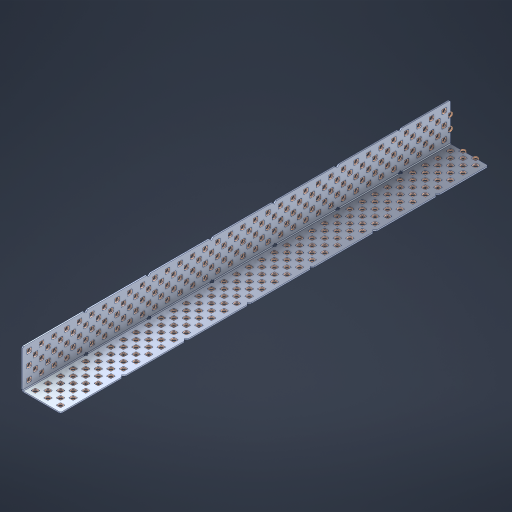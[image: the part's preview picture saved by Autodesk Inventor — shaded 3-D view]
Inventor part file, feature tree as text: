
AUTODESK INVENTOR PART (.ipt)
format: ipt  version: 2023 (Build 270158000, 158)  size: 3,338,752 bytes
history: native  units: in
note: dims shown in document units (in); Inventor stores cm internally (conversion verified against a paired STEP export)
features: other x346, extrude x338, sheet_metal_op x8, sketch x7, pattern_linear x3, mirror x1, chamfer x1
ambient origin geometry x8: Origin, YZ Plane, XZ Plane, XY Plane, X Axis, Y Axis, Z Axis, Center Point
bodies: Solid1 (feature_tree), Body (feature_tree)
feature tree (704):
  sheet_metal_op  "Flanges"
  sheet_metal_op  "Body Pattern"
  pattern_linear  "Center Double"  Spacing1=1.5in  [1 undecoded]
  pattern_linear  "Center Pattern"  Spacing1=0.1875in  [1 undecoded]
  other  "Arc Length"
  pattern_linear  "Notch Pattern"  Spacing1=0.0469in  [1 undecoded]
  other  "Diagonal Plane"
  mirror  "Everything Mirrored"
  chamfer  "End Chamfer"
  sketch  "Sketch1"  dims[d0=1.5in]
  other  "Plate1"
  sketch  "Sketch2"  dims[d1=17.0in]
  other  "Plate2"
  sheet_metal_op  "Bend1"
  sheet_metal_op  "Corner1"
  sketch  "Sketch8"  dims[d2=0.0469in]
  sketch  "Sketch9"  dims[d3=0.0469in]
  other  "Srf91"
  sheet_metal_op  "Body Pattern Sketch"
  other  "Srf92"
  sketch  "Sketch13"  dims[d4=0.0234in]
  sketch  "Sketch15"  dims[d5=0.0938in]
  sketch  "Sketch16"  dims[d6=0.0469in d7=1.5in d8=90.0deg d9=0.0312in d10=0.1875in d11=0.0469in d12=0.0469in d49=0.182in d50=0.02in d52=0.25in d53=0.0469in d54=0.0in d55=0.172in d56=1.0in d57=0.0in d85=0.1473in d86=0.1659in d89=0.0469in d90=0.0in d91=0.04in d92=0.0491in d95=2.5in d96=0.04in d97=0.25in d98=45.0deg d106=0.182in d107=0.02in d110=0.0469in d111=0.0in d112=0.172in d113=0.5in d114=0.0in d117=0.5in d126=0.0491in d127=0.1227in d128=0.08in d129=0.04in d130=2.5in d131=0.25in d132=13.3858in d134=0.5in d135=1.1811in d137=0.5in d140=0.5in d141=1.0in d142=0.3937in d144=0.5in d145=0.071in d146=0.7874in d148=0.5in]
  other  "Srf786"
  other  "Srf856"
  other  "Srf889"
  other  "Srf890"
  other  "Srf891"
  other  "Srf1275"
  other  "Srf1276"
  other  "Srf1278"
  other  "Srf1277"
  other  "Srf1285"
  other  "Srf1286"
  other  "Srf1287"
  other  "Srf1445"
  other  "Srf1446"
  other  "Srf1447"
  other  "Srf1448"
  other  "Srf1449"
  other  "Srf1537"
  other  "Srf1538"
  other  "Srf1539"
  other  "Srf1540"
  other  "Srf1541"
  other  "Srf1807"
  other  "Srf1808"
  other  "Srf1809"
  other  "Srf1810"
  other  "Srf1811"
  other  "Srf1812"
  other  "Srf1813"
  other  "Srf1814"
  other  "Srf1815"
  other  "Srf1816"
  other  "Srf1817"
  other  "Srf1818"
  other  "Srf1819"
  other  "Srf1820"
  other  "Srf1821"
  other  "Srf1822"
  other  "Srf1823"
  other  "Srf1824"
  other  "Srf1825"
  other  "Srf1826"
  other  "Srf1827"
  other  "Srf1828"
  other  "Srf1829"
  other  "Srf1830"
  other  "Srf1831"
  other  "Srf1959"
  other  "Srf1960"
  other  "Srf1961"
  other  "Srf1962"
  other  "Srf1963"
  other  "Srf1964"
  other  "Srf1965"
  other  "Srf1966"
  other  "Srf1967"
  other  "Srf1968"
  other  "Srf1969"
  other  "Srf1970"
  other  "Srf1971"
  other  "Srf1972"
  other  "Srf1973"
  other  "Srf1974"
  other  "Srf1975"
  other  "Srf1976"
  other  "Srf1977"
  other  "Srf1978"
  other  "Srf1979"
  other  "Srf1980"
  other  "Srf1981"
  other  "Srf1982"
  other  "Srf1983"
  other  "Srf2009"
  other  "Srf2010"
  other  "Srf2011"
  other  "Srf2012"
  other  "Srf2013"
  other  "Srf2014"
  other  "Srf2015"
  other  "Srf2016"
  other  "Srf2017"
  other  "Srf2018"
  other  "Srf2019"
  other  "Srf2020"
  other  "Srf2021"
  other  "Srf2022"
  other  "Srf2023"
  other  "Srf2024"
  other  "Srf2025"
  other  "Srf2026"
  other  "Srf2027"
  other  "Srf2028"
  other  "Srf2029"
  other  "Srf2030"
  other  "Srf2031"
  other  "Srf2032"
  other  "Srf2033"
  other  "Srf2034"
  other  "Srf2035"
  other  "Srf2036"
  other  "Srf2037"
  other  "Srf2038"
  other  "Srf2039"
  other  "Srf2040"
  other  "Srf2041"
  other  "Srf2042"
  other  "Srf2043"
  other  "Srf2044"
  other  "Srf2045"
  other  "Srf2046"
  other  "Srf2047"
  other  "Srf2048"
  other  "Srf2049"
  other  "Srf2050"
  other  "Srf2051"
  other  "Srf2052"
  other  "Srf2053"
  other  "Srf2054"
  other  "Srf2055"
  other  "Srf2056"
  other  "Srf2057"
  other  "Srf2058"
  other  "Srf2059"
  other  "Srf2060"
  other  "Srf2061"
  other  "Srf2062"
  other  "Srf2063"
  other  "Srf2064"
  other  "Srf2065"
  other  "Srf2066"
  other  "Srf2067"
  other  "Srf2068"
  other  "Srf2069"
  other  "Srf2070"
  other  "Srf2071"
  other  "Srf2072"
  other  "Srf2073"
  other  "Srf2074"
  other  "Srf2075"
  other  "Srf2076"
  other  "Srf2077"
  other  "Srf2078"
  other  "Srf2079"
  other  "Srf2080"
  other  "Srf2081"
  other  "Srf2082"
  other  "Srf2083"
  other  "Srf2084"
  other  "Srf2085"
  other  "Srf2086"
  other  "Srf2087"
  other  "Srf2088"
  other  "Srf2089"
  other  "Srf2090"
  other  "Srf2091"
  other  "Srf2092"
  other  "Srf2093"
  other  "Srf2094"
  other  "Srf2095"
  other  "Srf2096"
  other  "Srf2097"
  other  "Srf2098"
  other  "Srf2099"
  other  "Srf2100"
  other  "Srf2101"
  other  "Srf2102"
  other  "Srf2103"
  other  "Srf2104"
  other  "Srf2105"
  other  "Srf2106"
  other  "Srf2107"
  other  "Srf2108"
  other  "Srf2109"
  other  "Srf2110"
  other  "Srf2111"
  other  "Srf2112"
  other  "Srf2113"
  other  "Srf2114"
  other  "Srf2115"
  other  "Srf2116"
  other  "Srf2117"
  other  "Srf2118"
  other  "Srf2119"
  other  "Srf2120"
  other  "Srf2121"
  other  "Srf2122"
  other  "Srf2123"
  other  "Srf2124"
  other  "Srf2125"
  other  "Srf2126"
  other  "Srf2127"
  other  "Srf2128"
  other  "Srf2129"
  other  "Srf2130"
  other  "Srf2131"
  other  "Srf2132"
  other  "Srf2133"
  other  "Srf2134"
  other  "Srf2135"
  other  "Srf2136"
  other  "Srf2137"
  other  "Srf2138"
  other  "Srf2139"
  other  "Srf2140"
  other  "Srf2141"
  other  "Srf2142"
  other  "Srf2143"
  other  "Srf2144"
  other  "Srf2145"
  other  "Srf2146"
  other  "Srf2147"
  other  "Srf2148"
  other  "Srf2149"
  other  "Srf2150"
  other  "Srf2151"
  other  "Srf2152"
  other  "Srf2153"
  other  "Srf2154"
  other  "Srf2155"
  other  "Srf2156"
  other  "Srf2157"
  other  "Srf2158"
  other  "Srf2159"
  other  "Srf2160"
  other  "Srf2161"
  other  "Srf2162"
  other  "Srf2163"
  other  "Srf2164"
  other  "Srf2165"
  other  "Srf2166"
  other  "Srf2167"
  other  "Srf2168"
  other  "Srf2169"
  other  "Srf2170"
  other  "Srf2171"
  other  "Srf2172"
  other  "Srf2173"
  other  "Srf2174"
  other  "Srf2175"
  other  "Srf2179"
  other  "Srf2180"
  other  "Srf2181"
  other  "Srf2182"
  other  "Srf2183"
  other  "Srf2184"
  other  "Srf2185"
  other  "Srf2186"
  other  "Srf2187"
  other  "Srf2188"
  other  "Srf2189"
  other  "Srf2190"
  other  "Srf2191"
  other  "Srf2192"
  other  "Srf2193"
  other  "Srf2194"
  other  "Srf2195"
  other  "Srf2196"
  other  "Srf2197"
  other  "Srf2198"
  other  "Srf2199"
  other  "Srf2200"
  other  "Srf2201"
  other  "Srf2202"
  other  "Srf2203"
  other  "Srf2204"
  other  "Srf2205"
  other  "Srf2206"
  other  "Srf2207"
  other  "Srf2208"
  other  "Srf2209"
  other  "Srf2210"
  other  "Srf2211"
  other  "Srf2212"
  other  "Srf2213"
  other  "Srf2214"
  other  "Srf2215"
  other  "Srf2216"
  other  "Srf2217"
  other  "Srf2218"
  other  "Srf2219"
  other  "Srf2220"
  other  "Srf2221"
  other  "Srf2222"
  other  "Srf2223"
  other  "Srf2224"
  other  "Srf2225"
  other  "Srf2226"
  other  "Srf2227"
  other  "Srf2228"
  other  "Srf2229"
  other  "Srf2230"
  other  "Srf2231"
  other  "Srf2232"
  other  "Srf2233"
  other  "Srf2234"
  other  "Srf2235"
  other  "Srf2236"
  other  "Srf2237"
  other  "Srf2238"
  other  "Srf2239"
  other  "Srf2240"
  other  "Srf2241"
  other  "Srf2242"
  other  "Srf2243"
  other  "Srf2244"
  other  "Srf2245"
  other  "Srf2246"
  other  "Srf2247"
  other  "Srf2248"
  other  "Srf2249"
  other  "Srf2250"
  other  "Srf2251"
  other  "Srf2252"
  other  "Srf2253"
  other  "Srf2254"
  other  "Srf2255"
  other  "Srf2256"
  other  "Srf2257"
  other  "Srf2258"
  other  "Srf2259"
  other  "Srf2260"
  other  "Srf2261"
  other  "Srf2262"
  other  "Srf2263"
  other  "Srf2264"
  other  "Srf2265"
  other  "Srf2266"
  other  "Srf2267"
  other  "Srf2268"
  other  "Srf2269"
  other  "Srf2270"
  other  "Srf2271"
  other  "Srf2272"
  other  "Srf2273"
  other  "Srf2274"
  other  "Srf2275"
  other  "Srf2276"
  other  "Srf2277"
  sheet_metal_op  "Body Stamp"
  sheet_metal_op  "Body Circle"
  other  "Center Stamp"
  other  "Center Circle"
  sheet_metal_op  "Notch"
  extrude  "ExtrusionSrf92"  Depth=0.0469in
  extrude  "ExtrusionSrf856"  Depth=0.182in
  extrude  "ExtrusionSrf889"  Depth=0.02in
  extrude  "ExtrusionSrf890"  Depth=0.25in
  extrude  "ExtrusionSrf891"  Depth=0.0469in
  extrude  "ExtrusionSrf1275"  TaperAngle=0.0deg  [1 undecoded]
  extrude  "ExtrusionSrf1276"  Depth=0.5in
  extrude  "ExtrusionSrf1277"  Depth=1.0in TaperAngle=0.0deg
  extrude  "ExtrusionSrf1345"  Depth=0.5in
  extrude  "ExtrusionSrf1346"  Depth=0.5in
  extrude  "ExtrusionSrf1347"  Depth=0.0469in
  extrude  "ExtrusionSrf1348"  Depth=0.5in TaperAngle=0.0deg
  extrude  "ExtrusionSrf1445"  Depth=0.5in
  extrude  "ExtrusionSrf1446"  Depth=0.25in TaperAngle=45.0deg
  extrude  "ExtrusionSrf1447"  Depth=0.182in
  extrude  "ExtrusionSrf1448"  Depth=0.02in
  extrude  "ExtrusionSrf1449"  Depth=0.0469in
  extrude  "ExtrusionSrf1537"  TaperAngle=0.0deg  [1 undecoded]
  extrude  "ExtrusionSrf1538"  Depth=0.5in
  extrude  "ExtrusionSrf1539"  Depth=0.5in TaperAngle=0.0deg
  extrude  "ExtrusionSrf1540"  Depth=0.5in
  extrude  "ExtrusionSrf1541"  Depth=0.5in
  extrude  "ExtrusionSrf1807"  Depth=0.5in
  extrude  "ExtrusionSrf1808"  Depth=0.5in
  extrude  "ExtrusionSrf1809"  Depth=0.5in
  extrude  "ExtrusionSrf1810"  Depth=0.5in
  extrude  "ExtrusionSrf1811"  Depth=0.25in
  extrude  "ExtrusionSrf1812"  Depth=0.5in
  extrude  "ExtrusionSrf1813"  Depth=0.5in
  extrude  "ExtrusionSrf1814"  Depth=0.5in
  extrude  "ExtrusionSrf1815"  Depth=1.0in
  extrude  "ExtrusionSrf1816"  Depth=0.3937in
  extrude  "ExtrusionSrf1817"  Depth=0.5in
  extrude  "ExtrusionSrf1818"  Depth=0.5in
  extrude  "ExtrusionSrf1819"  [1 undecoded]
  extrude  "ExtrusionSrf1820"  [1 undecoded]
  extrude  "ExtrusionSrf1821"  [1 undecoded]
  extrude  "ExtrusionSrf1822"  [1 undecoded]
  extrude  "ExtrusionSrf1823"  [1 undecoded]
  extrude  "ExtrusionSrf1824"  [1 undecoded]
  extrude  "ExtrusionSrf1825"  [1 undecoded]
  extrude  "ExtrusionSrf1826"  [1 undecoded]
  extrude  "ExtrusionSrf1827"  [1 undecoded]
  extrude  "ExtrusionSrf1828"  [1 undecoded]
  extrude  "ExtrusionSrf1829"  [1 undecoded]
  extrude  "ExtrusionSrf1830"  [1 undecoded]
  extrude  "ExtrusionSrf1831"  [1 undecoded]
  extrude  "ExtrusionSrf1959"  [1 undecoded]
  extrude  "ExtrusionSrf1960"  [1 undecoded]
  extrude  "ExtrusionSrf1961"  [1 undecoded]
  extrude  "ExtrusionSrf1962"  [1 undecoded]
  extrude  "ExtrusionSrf1963"  [1 undecoded]
  extrude  "ExtrusionSrf1964"  [1 undecoded]
  extrude  "ExtrusionSrf1965"  [1 undecoded]
  extrude  "ExtrusionSrf1966"  [1 undecoded]
  extrude  "ExtrusionSrf1967"  [1 undecoded]
  extrude  "ExtrusionSrf1968"  [1 undecoded]
  extrude  "ExtrusionSrf1969"  [1 undecoded]
  extrude  "ExtrusionSrf1970"  [1 undecoded]
  extrude  "ExtrusionSrf1971"  [1 undecoded]
  extrude  "ExtrusionSrf1972"  [1 undecoded]
  extrude  "ExtrusionSrf1973"  [1 undecoded]
  extrude  "ExtrusionSrf1974"  [1 undecoded]
  extrude  "ExtrusionSrf1975"  [1 undecoded]
  extrude  "ExtrusionSrf1976"  [1 undecoded]
  extrude  "ExtrusionSrf1977"  [1 undecoded]
  extrude  "ExtrusionSrf1978"  [1 undecoded]
  extrude  "ExtrusionSrf1979"  [1 undecoded]
  extrude  "ExtrusionSrf1980"  [1 undecoded]
  extrude  "ExtrusionSrf1981"  [1 undecoded]
  extrude  "ExtrusionSrf1982"  [1 undecoded]
  extrude  "ExtrusionSrf1983"  [1 undecoded]
  extrude  "ExtrusionSrf2009"  [1 undecoded]
  extrude  "ExtrusionSrf2010"  [1 undecoded]
  extrude  "ExtrusionSrf2011"  [1 undecoded]
  extrude  "ExtrusionSrf2012"  [1 undecoded]
  extrude  "ExtrusionSrf2013"  [1 undecoded]
  extrude  "ExtrusionSrf2014"  [1 undecoded]
  extrude  "ExtrusionSrf2015"  [1 undecoded]
  extrude  "ExtrusionSrf2016"  [1 undecoded]
  extrude  "ExtrusionSrf2017"  [1 undecoded]
  extrude  "ExtrusionSrf2018"  [1 undecoded]
  extrude  "ExtrusionSrf2019"  [1 undecoded]
  extrude  "ExtrusionSrf2020"  [1 undecoded]
  extrude  "ExtrusionSrf2021"  [1 undecoded]
  extrude  "ExtrusionSrf2022"  [1 undecoded]
  extrude  "ExtrusionSrf2023"  [1 undecoded]
  extrude  "ExtrusionSrf2024"  [1 undecoded]
  extrude  "ExtrusionSrf2025"  [1 undecoded]
  extrude  "ExtrusionSrf2026"  [1 undecoded]
  extrude  "ExtrusionSrf2027"  [1 undecoded]
  extrude  "ExtrusionSrf2028"  [1 undecoded]
  extrude  "ExtrusionSrf2029"  [1 undecoded]
  extrude  "ExtrusionSrf2030"  [1 undecoded]
  extrude  "ExtrusionSrf2031"  [1 undecoded]
  extrude  "ExtrusionSrf2032"  [1 undecoded]
  extrude  "ExtrusionSrf2033"  [1 undecoded]
  extrude  "ExtrusionSrf2034"  [1 undecoded]
  extrude  "ExtrusionSrf2035"  [1 undecoded]
  extrude  "ExtrusionSrf2036"  [1 undecoded]
  extrude  "ExtrusionSrf2037"  [1 undecoded]
  extrude  "ExtrusionSrf2038"  [1 undecoded]
  extrude  "ExtrusionSrf2039"  [1 undecoded]
  extrude  "ExtrusionSrf2040"  [1 undecoded]
  extrude  "ExtrusionSrf2041"  [1 undecoded]
  extrude  "ExtrusionSrf2042"  [1 undecoded]
  extrude  "ExtrusionSrf2043"  [1 undecoded]
  extrude  "ExtrusionSrf2044"  [1 undecoded]
  extrude  "ExtrusionSrf2045"  [1 undecoded]
  extrude  "ExtrusionSrf2046"  [1 undecoded]
  extrude  "ExtrusionSrf2047"  [1 undecoded]
  extrude  "ExtrusionSrf2048"  [1 undecoded]
  extrude  "ExtrusionSrf2049"  [1 undecoded]
  extrude  "ExtrusionSrf2050"  [1 undecoded]
  extrude  "ExtrusionSrf2051"  [1 undecoded]
  extrude  "ExtrusionSrf2052"  [1 undecoded]
  extrude  "ExtrusionSrf2053"  [1 undecoded]
  extrude  "ExtrusionSrf2054"  [1 undecoded]
  extrude  "ExtrusionSrf2055"  [1 undecoded]
  extrude  "ExtrusionSrf2056"  [1 undecoded]
  extrude  "ExtrusionSrf2057"  [1 undecoded]
  extrude  "ExtrusionSrf2058"  [1 undecoded]
  extrude  "ExtrusionSrf2059"  [1 undecoded]
  extrude  "ExtrusionSrf2060"  [1 undecoded]
  extrude  "ExtrusionSrf2061"  [1 undecoded]
  extrude  "ExtrusionSrf2062"  [1 undecoded]
  extrude  "ExtrusionSrf2063"  [1 undecoded]
  extrude  "ExtrusionSrf2064"  [1 undecoded]
  extrude  "ExtrusionSrf2065"  [1 undecoded]
  extrude  "ExtrusionSrf2066"  [1 undecoded]
  extrude  "ExtrusionSrf2067"  [1 undecoded]
  extrude  "ExtrusionSrf2068"  [1 undecoded]
  extrude  "ExtrusionSrf2069"  [1 undecoded]
  extrude  "ExtrusionSrf2070"  [1 undecoded]
  extrude  "ExtrusionSrf2071"  [1 undecoded]
  extrude  "ExtrusionSrf2072"  [1 undecoded]
  extrude  "ExtrusionSrf2073"  [1 undecoded]
  extrude  "ExtrusionSrf2074"  [1 undecoded]
  extrude  "ExtrusionSrf2075"  [1 undecoded]
  extrude  "ExtrusionSrf2076"  [1 undecoded]
  extrude  "ExtrusionSrf2077"  [1 undecoded]
  extrude  "ExtrusionSrf2078"  [1 undecoded]
  extrude  "ExtrusionSrf2079"  [1 undecoded]
  extrude  "ExtrusionSrf2080"  [1 undecoded]
  extrude  "ExtrusionSrf2081"  [1 undecoded]
  extrude  "ExtrusionSrf2082"  [1 undecoded]
  extrude  "ExtrusionSrf2083"  [1 undecoded]
  extrude  "ExtrusionSrf2084"  [1 undecoded]
  extrude  "ExtrusionSrf2085"  [1 undecoded]
  extrude  "ExtrusionSrf2086"  [1 undecoded]
  extrude  "ExtrusionSrf2087"  [1 undecoded]
  extrude  "ExtrusionSrf2088"  [1 undecoded]
  extrude  "ExtrusionSrf2089"  [1 undecoded]
  extrude  "ExtrusionSrf2090"  [1 undecoded]
  extrude  "ExtrusionSrf2091"  [1 undecoded]
  extrude  "ExtrusionSrf2092"  [1 undecoded]
  extrude  "ExtrusionSrf2093"  [1 undecoded]
  extrude  "ExtrusionSrf2094"  [1 undecoded]
  extrude  "ExtrusionSrf2095"  [1 undecoded]
  extrude  "ExtrusionSrf2096"  [1 undecoded]
  extrude  "ExtrusionSrf2097"  [1 undecoded]
  extrude  "ExtrusionSrf2098"  [1 undecoded]
  extrude  "ExtrusionSrf2099"  [1 undecoded]
  extrude  "ExtrusionSrf2100"  [1 undecoded]
  extrude  "ExtrusionSrf2101"  [1 undecoded]
  extrude  "ExtrusionSrf2102"  [1 undecoded]
  extrude  "ExtrusionSrf2103"  [1 undecoded]
  extrude  "ExtrusionSrf2104"  [1 undecoded]
  extrude  "ExtrusionSrf2105"  [1 undecoded]
  extrude  "ExtrusionSrf2106"  [1 undecoded]
  extrude  "ExtrusionSrf2107"  [1 undecoded]
  extrude  "ExtrusionSrf2108"  [1 undecoded]
  extrude  "ExtrusionSrf2109"  [1 undecoded]
  extrude  "ExtrusionSrf2110"  [1 undecoded]
  extrude  "ExtrusionSrf2111"  [1 undecoded]
  extrude  "ExtrusionSrf2112"  [1 undecoded]
  extrude  "ExtrusionSrf2113"  [1 undecoded]
  extrude  "ExtrusionSrf2114"  [1 undecoded]
  extrude  "ExtrusionSrf2115"  [1 undecoded]
  extrude  "ExtrusionSrf2116"  [1 undecoded]
  extrude  "ExtrusionSrf2117"  [1 undecoded]
  extrude  "ExtrusionSrf2118"  [1 undecoded]
  extrude  "ExtrusionSrf2119"  [1 undecoded]
  extrude  "ExtrusionSrf2120"  [1 undecoded]
  extrude  "ExtrusionSrf2121"  [1 undecoded]
  extrude  "ExtrusionSrf2122"  [1 undecoded]
  extrude  "ExtrusionSrf2123"  [1 undecoded]
  extrude  "ExtrusionSrf2124"  [1 undecoded]
  extrude  "ExtrusionSrf2125"  [1 undecoded]
  extrude  "ExtrusionSrf2126"  [1 undecoded]
  extrude  "ExtrusionSrf2127"  [1 undecoded]
  extrude  "ExtrusionSrf2128"  [1 undecoded]
  extrude  "ExtrusionSrf2129"  [1 undecoded]
  extrude  "ExtrusionSrf2130"  [1 undecoded]
  extrude  "ExtrusionSrf2131"  [1 undecoded]
  extrude  "ExtrusionSrf2132"  [1 undecoded]
  extrude  "ExtrusionSrf2133"  [1 undecoded]
  extrude  "ExtrusionSrf2134"  [1 undecoded]
  extrude  "ExtrusionSrf2135"  [1 undecoded]
  extrude  "ExtrusionSrf2136"  [1 undecoded]
  extrude  "ExtrusionSrf2137"  [1 undecoded]
  extrude  "ExtrusionSrf2138"  [1 undecoded]
  extrude  "ExtrusionSrf2139"  [1 undecoded]
  extrude  "ExtrusionSrf2140"  [1 undecoded]
  extrude  "ExtrusionSrf2141"  [1 undecoded]
  extrude  "ExtrusionSrf2142"  [1 undecoded]
  extrude  "ExtrusionSrf2143"  [1 undecoded]
  extrude  "ExtrusionSrf2144"  [1 undecoded]
  extrude  "ExtrusionSrf2145"  [1 undecoded]
  extrude  "ExtrusionSrf2146"  [1 undecoded]
  extrude  "ExtrusionSrf2147"  [1 undecoded]
  extrude  "ExtrusionSrf2148"  [1 undecoded]
  extrude  "ExtrusionSrf2149"  [1 undecoded]
  extrude  "ExtrusionSrf2150"  [1 undecoded]
  extrude  "ExtrusionSrf2151"  [1 undecoded]
  extrude  "ExtrusionSrf2152"  [1 undecoded]
  extrude  "ExtrusionSrf2153"  [1 undecoded]
  extrude  "ExtrusionSrf2154"  [1 undecoded]
  extrude  "ExtrusionSrf2155"  [1 undecoded]
  extrude  "ExtrusionSrf2156"  [1 undecoded]
  extrude  "ExtrusionSrf2157"  [1 undecoded]
  extrude  "ExtrusionSrf2158"  [1 undecoded]
  extrude  "ExtrusionSrf2159"  [1 undecoded]
  extrude  "ExtrusionSrf2160"  [1 undecoded]
  extrude  "ExtrusionSrf2161"  [1 undecoded]
  extrude  "ExtrusionSrf2162"  [1 undecoded]
  extrude  "ExtrusionSrf2163"  [1 undecoded]
  extrude  "ExtrusionSrf2164"  [1 undecoded]
  extrude  "ExtrusionSrf2165"  [1 undecoded]
  extrude  "ExtrusionSrf2166"  [1 undecoded]
  extrude  "ExtrusionSrf2167"  [1 undecoded]
  extrude  "ExtrusionSrf2168"  [1 undecoded]
  extrude  "ExtrusionSrf2169"  [1 undecoded]
  extrude  "ExtrusionSrf2170"  [1 undecoded]
  extrude  "ExtrusionSrf2171"  [1 undecoded]
  extrude  "ExtrusionSrf2172"  [1 undecoded]
  extrude  "ExtrusionSrf2173"  [1 undecoded]
  extrude  "ExtrusionSrf2174"  [1 undecoded]
  extrude  "ExtrusionSrf2175"  [1 undecoded]
  extrude  "ExtrusionSrf2179"  [1 undecoded]
  extrude  "ExtrusionSrf2180"  [1 undecoded]
  extrude  "ExtrusionSrf2181"  [1 undecoded]
  extrude  "ExtrusionSrf2182"  [1 undecoded]
  extrude  "ExtrusionSrf2183"  [1 undecoded]
  extrude  "ExtrusionSrf2184"  [1 undecoded]
  extrude  "ExtrusionSrf2185"  [1 undecoded]
  extrude  "ExtrusionSrf2186"  [1 undecoded]
  extrude  "ExtrusionSrf2187"  [1 undecoded]
  extrude  "ExtrusionSrf2188"  [1 undecoded]
  extrude  "ExtrusionSrf2189"  [1 undecoded]
  extrude  "ExtrusionSrf2190"  [1 undecoded]
  extrude  "ExtrusionSrf2191"  [1 undecoded]
  extrude  "ExtrusionSrf2192"  [1 undecoded]
  extrude  "ExtrusionSrf2193"  [1 undecoded]
  extrude  "ExtrusionSrf2194"  [1 undecoded]
  extrude  "ExtrusionSrf2195"  [1 undecoded]
  extrude  "ExtrusionSrf2196"  [1 undecoded]
  extrude  "ExtrusionSrf2197"  [1 undecoded]
  extrude  "ExtrusionSrf2198"  [1 undecoded]
  extrude  "ExtrusionSrf2199"  [1 undecoded]
  extrude  "ExtrusionSrf2200"  [1 undecoded]
  extrude  "ExtrusionSrf2201"  [1 undecoded]
  extrude  "ExtrusionSrf2202"  [1 undecoded]
  extrude  "ExtrusionSrf2203"  [1 undecoded]
  extrude  "ExtrusionSrf2204"  [1 undecoded]
  extrude  "ExtrusionSrf2205"  [1 undecoded]
  extrude  "ExtrusionSrf2206"  [1 undecoded]
  extrude  "ExtrusionSrf2207"  [1 undecoded]
  extrude  "ExtrusionSrf2208"  [1 undecoded]
  extrude  "ExtrusionSrf2209"  [1 undecoded]
  extrude  "ExtrusionSrf2210"  [1 undecoded]
  extrude  "ExtrusionSrf2211"  [1 undecoded]
  extrude  "ExtrusionSrf2212"  [1 undecoded]
  extrude  "ExtrusionSrf2213"  [1 undecoded]
  extrude  "ExtrusionSrf2214"  [1 undecoded]
  extrude  "ExtrusionSrf2215"  [1 undecoded]
  extrude  "ExtrusionSrf2216"  [1 undecoded]
  extrude  "ExtrusionSrf2217"  [1 undecoded]
  extrude  "ExtrusionSrf2218"  [1 undecoded]
  extrude  "ExtrusionSrf2219"  [1 undecoded]
  extrude  "ExtrusionSrf2220"  [1 undecoded]
  extrude  "ExtrusionSrf2221"  [1 undecoded]
  extrude  "ExtrusionSrf2222"  [1 undecoded]
  extrude  "ExtrusionSrf2223"  [1 undecoded]
  extrude  "ExtrusionSrf2224"  [1 undecoded]
  extrude  "ExtrusionSrf2225"  [1 undecoded]
  extrude  "ExtrusionSrf2226"  [1 undecoded]
  extrude  "ExtrusionSrf2227"  [1 undecoded]
  extrude  "ExtrusionSrf2228"  [1 undecoded]
  extrude  "ExtrusionSrf2229"  [1 undecoded]
  extrude  "ExtrusionSrf2230"  [1 undecoded]
  extrude  "ExtrusionSrf2231"  [1 undecoded]
  extrude  "ExtrusionSrf2232"  [1 undecoded]
  extrude  "ExtrusionSrf2233"  [1 undecoded]
  extrude  "ExtrusionSrf2234"  [1 undecoded]
  extrude  "ExtrusionSrf2235"  [1 undecoded]
  extrude  "ExtrusionSrf2236"  [1 undecoded]
  extrude  "ExtrusionSrf2237"  [1 undecoded]
  extrude  "ExtrusionSrf2238"  [1 undecoded]
  extrude  "ExtrusionSrf2239"  [1 undecoded]
  extrude  "ExtrusionSrf2240"  [1 undecoded]
  extrude  "ExtrusionSrf2241"  [1 undecoded]
  extrude  "ExtrusionSrf2242"  [1 undecoded]
  extrude  "ExtrusionSrf2243"  [1 undecoded]
  extrude  "ExtrusionSrf2244"  [1 undecoded]
  extrude  "ExtrusionSrf2245"  [1 undecoded]
  extrude  "ExtrusionSrf2246"  [1 undecoded]
  extrude  "ExtrusionSrf2247"  [1 undecoded]
  extrude  "ExtrusionSrf2248"  [1 undecoded]
  extrude  "ExtrusionSrf2249"  [1 undecoded]
  extrude  "ExtrusionSrf2250"  [1 undecoded]
  extrude  "ExtrusionSrf2251"  [1 undecoded]
  extrude  "ExtrusionSrf2252"  [1 undecoded]
  extrude  "ExtrusionSrf2253"  [1 undecoded]
  extrude  "ExtrusionSrf2254"  [1 undecoded]
  extrude  "ExtrusionSrf2255"  [1 undecoded]
  extrude  "ExtrusionSrf2256"  [1 undecoded]
  extrude  "ExtrusionSrf2257"  [1 undecoded]
  extrude  "ExtrusionSrf2258"  [1 undecoded]
  extrude  "ExtrusionSrf2259"  [1 undecoded]
  extrude  "ExtrusionSrf2260"  [1 undecoded]
  extrude  "ExtrusionSrf2261"  [1 undecoded]
  extrude  "ExtrusionSrf2262"  [1 undecoded]
  extrude  "ExtrusionSrf2263"  [1 undecoded]
  extrude  "ExtrusionSrf2264"  [1 undecoded]
  extrude  "ExtrusionSrf2265"  [1 undecoded]
  extrude  "ExtrusionSrf2266"  [1 undecoded]
  extrude  "ExtrusionSrf2267"  [1 undecoded]
  extrude  "ExtrusionSrf2268"  [1 undecoded]
  extrude  "ExtrusionSrf2269"  [1 undecoded]
  extrude  "ExtrusionSrf2270"  [1 undecoded]
  extrude  "ExtrusionSrf2271"  [1 undecoded]
  extrude  "ExtrusionSrf2272"  [1 undecoded]
  extrude  "ExtrusionSrf2273"  [1 undecoded]
  extrude  "ExtrusionSrf2274"  [1 undecoded]
  extrude  "ExtrusionSrf2275"  [1 undecoded]
  extrude  "ExtrusionSrf2276"  [1 undecoded]
  extrude  "ExtrusionSrf2277"  [1 undecoded]
note: 309 required parameter values undecoded (feature->parameter linkage not recoverable at this tier; creation-order binding heuristic only, values carry confidence <= 0.55)
